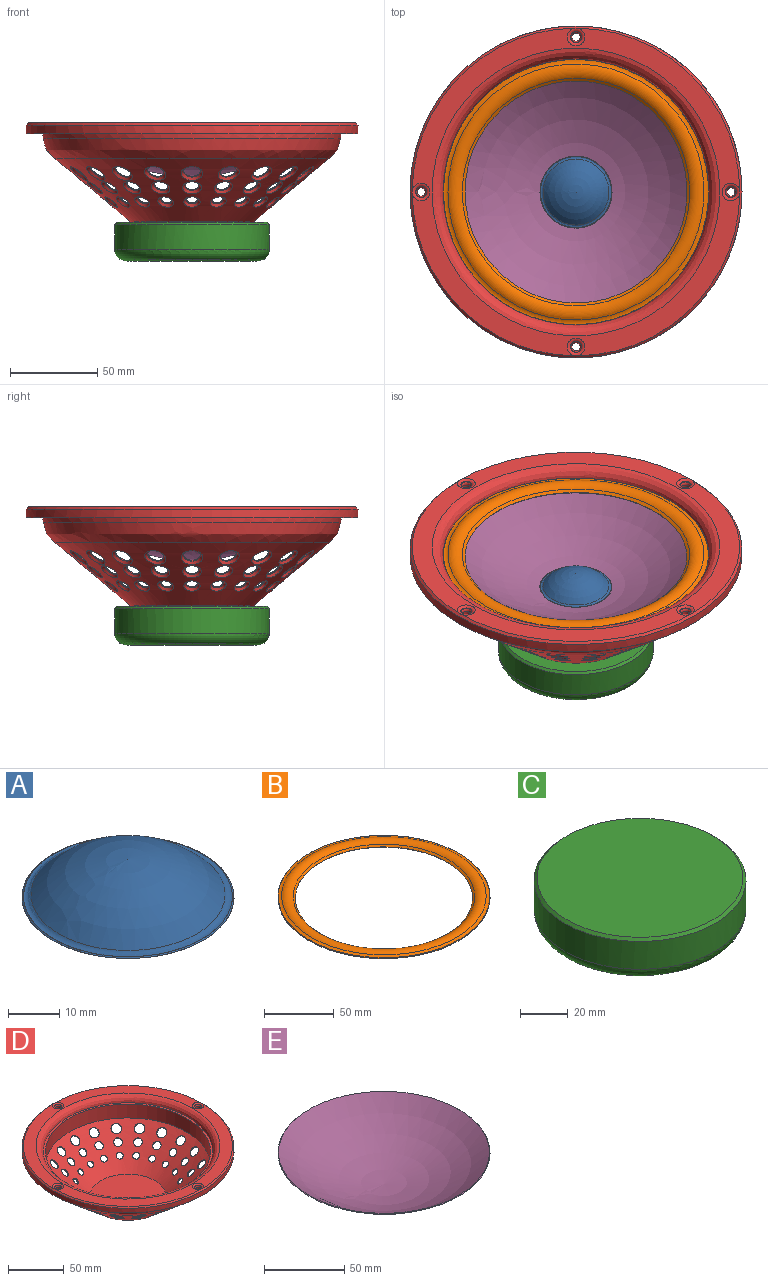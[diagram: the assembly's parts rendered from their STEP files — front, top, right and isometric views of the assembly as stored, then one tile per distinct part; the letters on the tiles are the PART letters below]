
ASSEMBLY  parts=5 mates=4
PART A: 7 faces, bbox 45.8x45.8x9.6 mm
  f0: sphere r=24.38mm, area 1308.1mm2, adj f1
  f1: sphere r=101.6mm, area 270.8mm2, adj f0,f2
  f2: cone r=20.64mm half-angle=11.7deg, axis (0,0,-1), area 0mm2, adj f1,f5
  f3: sphere r=101.35mm, area 2.8mm2, adj f5,f6
  f4: sphere r=25.4mm, area 1350.2mm2, adj f6
  f5: cone r=20.69mm half-angle=56.7deg, axis (0,0,-1), area 46.3mm2, adj f2,f3
  f6: torus R=20.06mm, axis (0,0,-1), area 195.8mm2, adj f3,f4
PART B: 9 faces, bbox 164.6x164.6x3.6 mm
  f0: torus R=69.85mm, axis (0,0,-1), area 4050mm2, adj f1,f7
  f1: plane 152.4x152.4mm, normal (0,0,-1), area 959.9mm2, adj f0,f2
  f2: cylinder r=76.2mm len=152.4mm, axis (0,0,-1), area 364.8mm2, adj f1,f3
  f3: plane 152.4x152.4mm, normal (0,0,1), area 73.1mm2, adj f2,f8
  f4: torus R=69.85mm, axis (0,0,-1), area 3828.5mm2, adj f5,f8
  f5: sphere r=100.84mm, area 823.2mm2, adj f4,f6
  f6: cone r=63.69mm half-angle=39.2deg, axis (0,0,-1), area 306.1mm2, adj f5,f7
  f7: sphere r=101.6mm, area 835.7mm2, adj f0,f6
  f8: torus R=76.05mm, axis (0,0,-1), area 1270.7mm2, adj f3,f4
PART C: 9 faces, bbox 97.6x97.6x22.2 mm
  f0: plane 86.36x86.36mm, normal (0,0,1), area 5857.5mm2, adj f8
  f1: sphere r=6.35mm, area 50.7mm2, adj f5
  f2: plane 51.04x51.04mm, normal (0,0,-1), area 1863.5mm2, adj f5,f6
  f3: torus R=36.05mm, axis (0,0,-1), area 2515.9mm2, adj f6,f7
  f4: cylinder r=44.45mm len=88.9mm, axis (0,0,-1), area 3984mm2, adj f7,f8
  f5: torus R=7.62mm, axis (0,0,1), area 145mm2, adj f1,f2
  f6: torus R=25.52mm, axis (0,0,-1), area 638.6mm2, adj f2,f3
  f7: torus R=38.1mm, axis (0,0,1), area 2127.8mm2, adj f3,f4
  f8: cone r=44.45mm half-angle=45deg, axis (0,0,-1), area 494.4mm2, adj f0,f4
PART D: 150 faces, bbox 192.7x190.5x57.2 mm
  f0: cone r=74.17mm half-angle=50deg, axis (0,0,1), area 14734.7mm2, adj f2,f9,f21,f22,f23,f24,f25,f26
  f1: cone r=84.05mm half-angle=50deg, axis (0,0,1), area 14756.1mm2, adj f18,f81,f82,f83,f84,f85,f86,f87
  f2: plane 68.23x68.23mm, normal (0,0,1), area 3656.6mm2, adj f0
  f3: plane 68.7x68.7mm, normal (0,0,-1), area 3706.4mm2, adj f141
  f4: cone r=85.72mm half-angle=10deg, axis (0,0,1), area 1470.8mm2, adj f5,f18
  f5: plane 190.5x190.5mm, normal (0,0,-1), area 5344.2mm2, adj f4,f6,f10,f12,f14,f16
  f6: cylinder r=95.25mm len=190.5mm, axis (0,0,-1), area 3040.2mm2, adj f5,f19
  f7: plane 187.99x187.99mm, normal (0,0,1), area 6016.8mm2, adj f19,f20,f143,f145,f147,f149
  f8: plane 152.41x152.41mm, normal (0,0,1), area 961.6mm2, adj f9,f20
  f9: cylinder r=74.17mm len=148.34mm, axis (0,0,-1), area 7065mm2, adj f0,f8
  f10: cylinder r=2.38mm len=4.76mm, axis (0,0,1), area 54.5mm2, adj f5,f148
  f11: cone r=2.38mm half-angle=42.5deg, axis (0,0,1), area 5.2mm2, adj f148,f149
  f12: cylinder r=2.38mm len=4.76mm, axis (0,0,1), area 54.5mm2, adj f5,f146
  f13: cone r=2.38mm half-angle=42.5deg, axis (0,0,1), area 5.2mm2, adj f146,f147
  f14: cylinder r=2.38mm len=4.76mm, axis (0,0,1), area 54.5mm2, adj f5,f144
  f15: cone r=2.38mm half-angle=42.5deg, axis (0,0,1), area 5.2mm2, adj f144,f145
  f16: cylinder r=2.38mm len=4.76mm, axis (0,0,1), area 54.5mm2, adj f5,f142
  f17: cone r=2.38mm half-angle=42.5deg, axis (0,0,1), area 5.2mm2, adj f142,f143
  f18: bspline ~170.5x170.5mm, area 7033.8mm2, adj f1,f4
  f19: cone r=95.25mm half-angle=45deg, axis (0,0,-1), area 1067.7mm2, adj f6,f7
  f20: bspline ~165.1x165.1mm, area 4895.7mm2, adj f7,f8
  f21: cylinder r=4.76mm len=9.53mm, axis (0.64,0,-0.77), area 17.4mm2, adj f0,f140
  f22: cylinder r=3.97mm len=7.62mm, axis (-0.38,0.52,-0.77), area 14.9mm2, adj f0,f118
  f23: cylinder r=4.76mm len=9.1mm, axis (-0.38,0.52,-0.77), area 17.9mm2, adj f0,f119
  f24: cylinder r=3.17mm len=6.11mm, axis (-0.38,0.52,-0.77), area 11.5mm2, adj f0,f117
  f25: cylinder r=4.76mm len=9.1mm, axis (-0.52,0.38,-0.77), area 19.6mm2, adj f0,f116
  f26: cylinder r=3.17mm len=6.35mm, axis (0,0.64,-0.77), area 11.3mm2, adj f0,f123
  f27: cylinder r=4.76mm len=9.48mm, axis (-0.2,0.61,-0.77), area 18mm2, adj f0,f122
  f28: cylinder r=3.17mm len=6.35mm, axis (-0.2,0.61,-0.77), area 11.5mm2, adj f0,f120
  f29: cylinder r=3.97mm len=7.91mm, axis (-0.2,0.61,-0.77), area 14.3mm2, adj f0,f121
  f30: cylinder r=3.17mm len=6.34mm, axis (-0.61,0.2,-0.77), area 11.3mm2, adj f0,f111
  f31: cylinder r=4.76mm len=9.53mm, axis (-0.64,0,-0.77), area 17.7mm2, adj f0,f110
  f32: cylinder r=3.97mm len=7.94mm, axis (-0.64,0,-0.77), area 14.8mm2, adj f0,f109
  f33: cylinder r=3.17mm len=6.35mm, axis (-0.64,0,-0.77), area 11.7mm2, adj f0,f108
  f34: cylinder r=3.17mm len=6.1mm, axis (-0.52,0.38,-0.77), area 11.4mm2, adj f0,f114
  f35: cylinder r=3.97mm len=7.62mm, axis (-0.52,0.38,-0.77), area 16mm2, adj f0,f115
  f36: cylinder r=3.97mm len=7.92mm, axis (-0.61,0.2,-0.77), area 16mm2, adj f0,f112
  f37: cylinder r=4.76mm len=9.48mm, axis (-0.61,0.2,-0.77), area 19.4mm2, adj f0,f113
  f38: cylinder r=3.17mm len=6.35mm, axis (0.61,0.2,-0.77), area 11.3mm2, adj f0,f135
  f39: cylinder r=4.76mm len=9.06mm, axis (0.52,0.38,-0.77), area 16.4mm2, adj f0,f134
  f40: cylinder r=3.17mm len=6.12mm, axis (0.52,0.38,-0.77), area 12.7mm2, adj f0,f132
  f41: cylinder r=3.97mm len=7.59mm, axis (0.52,0.38,-0.77), area 13.9mm2, adj f0,f133
  f42: cylinder r=4.76mm len=9.46mm, axis (0.61,0.2,-0.77), area 16.8mm2, adj f0,f137
  f43: cylinder r=3.97mm len=7.91mm, axis (0.61,0.2,-0.77), area 13.8mm2, adj f0,f136
  f44: cylinder r=3.17mm len=6.35mm, axis (0.64,0,-0.77), area 11.3mm2, adj f0,f138
  f45: cylinder r=3.97mm len=7.94mm, axis (0.64,0,-0.77), area 13.9mm2, adj f0,f139
  f46: cylinder r=4.76mm len=9.53mm, axis (0,0.64,-0.77), area 17.3mm2, adj f0,f125
  f47: cylinder r=3.97mm len=7.94mm, axis (0,0.64,-0.77), area 13.9mm2, adj f0,f124
  f48: cylinder r=3.97mm len=7.91mm, axis (0.2,0.61,-0.77), area 13.8mm2, adj f0,f127
  f49: cylinder r=3.17mm len=6.35mm, axis (0.2,0.61,-0.77), area 11.3mm2, adj f0,f126
  f50: cylinder r=3.97mm len=7.59mm, axis (0.38,0.52,-0.77), area 13.9mm2, adj f0,f130
  f51: cylinder r=4.76mm len=9.06mm, axis (0.38,0.52,-0.77), area 16.4mm2, adj f0,f131
  f52: cylinder r=3.17mm len=6.12mm, axis (0.38,0.52,-0.77), area 12.7mm2, adj f0,f129
  f53: cylinder r=4.76mm len=9.46mm, axis (0.2,0.61,-0.77), area 16.8mm2, adj f0,f128
  f54: cylinder r=3.17mm len=6.13mm, axis (0.38,-0.52,-0.77), area 12.1mm2, adj f0,f87
  f55: cylinder r=4.76mm len=9.1mm, axis (0.52,-0.38,-0.77), area 18mm2, adj f0,f86
  f56: cylinder r=3.17mm len=6.13mm, axis (0.52,-0.38,-0.77), area 11.8mm2, adj f0,f84
  f57: cylinder r=3.97mm len=7.62mm, axis (0.52,-0.38,-0.77), area 14.9mm2, adj f0,f85
  f58: cylinder r=4.76mm len=9.1mm, axis (0.38,-0.52,-0.77), area 19.5mm2, adj f0,f89
  f59: cylinder r=3.97mm len=7.62mm, axis (0.38,-0.52,-0.77), area 16mm2, adj f0,f88
  f60: cylinder r=3.97mm len=7.92mm, axis (0.2,-0.61,-0.77), area 16mm2, adj f0,f91
  f61: cylinder r=3.17mm len=6.36mm, axis (0.2,-0.61,-0.77), area 12.3mm2, adj f0,f90
  f62: cylinder r=3.17mm len=6.35mm, axis (0.61,-0.2,-0.77), area 11.5mm2, adj f0,f81
  f63: cylinder r=4.76mm len=9.48mm, axis (0.61,-0.2,-0.77), area 17.9mm2, adj f0,f83
  f64: cylinder r=3.97mm len=7.91mm, axis (0.61,-0.2,-0.77), area 14.3mm2, adj f0,f82
  f65: cylinder r=4.76mm len=9.06mm, axis (-0.38,-0.52,-0.77), area 16.3mm2, adj f0,f101
  f66: cylinder r=3.97mm len=7.61mm, axis (-0.38,-0.52,-0.77), area 15.3mm2, adj f0,f100
  f67: cylinder r=3.97mm len=7.61mm, axis (-0.52,-0.38,-0.77), area 15.2mm2, adj f0,f103
  f68: cylinder r=3.17mm len=6.1mm, axis (-0.52,-0.38,-0.77), area 11.2mm2, adj f0,f102
  f69: cylinder r=3.97mm len=7.92mm, axis (-0.61,-0.2,-0.77), area 15.8mm2, adj f0,f106
  f70: cylinder r=4.76mm len=9.48mm, axis (-0.61,-0.2,-0.77), area 19.3mm2, adj f0,f107
  f71: cylinder r=3.17mm len=6.36mm, axis (-0.61,-0.2,-0.77), area 12.5mm2, adj f0,f105
  f72: cylinder r=4.76mm len=9.06mm, axis (-0.52,-0.38,-0.77), area 16.4mm2, adj f0,f104
  f73: cylinder r=3.97mm len=7.92mm, axis (-0.2,-0.61,-0.77), area 15.8mm2, adj f0,f97
  f74: cylinder r=3.17mm len=6.36mm, axis (-0.2,-0.61,-0.77), area 12.5mm2, adj f0,f96
  f75: cylinder r=4.76mm len=9.48mm, axis (-0.2,-0.61,-0.77), area 19.3mm2, adj f0,f98
  f76: cylinder r=3.17mm len=6.14mm, axis (-0.38,-0.52,-0.77), area 12.3mm2, adj f0,f99
  f77: cylinder r=4.76mm len=9.48mm, axis (0.2,-0.61,-0.77), area 19.5mm2, adj f0,f92
  f78: cylinder r=3.17mm len=6.35mm, axis (0,-0.64,-0.77), area 12.6mm2, adj f0,f93
  f79: cylinder r=4.76mm len=9.53mm, axis (0,-0.64,-0.77), area 19.5mm2, adj f0,f95
  f80: cylinder r=3.97mm len=7.94mm, axis (0,-0.64,-0.77), area 16.1mm2, adj f0,f94
  f81: bspline ~9.11x7.25mm, area 49mm2, adj f1,f62
  f82: bspline ~10.66x8.51mm, area 59mm2, adj f1,f64
  f83: bspline ~12.21x9.76mm, area 68.9mm2, adj f1,f63
  f84: bspline ~8.58x7.87mm, area 49mm2, adj f1,f56
  f85: bspline ~10.04x9.23mm, area 59mm2, adj f1,f57
  f86: bspline ~11.51x10.58mm, area 68.9mm2, adj f1,f55
  f87: bspline ~8.58x7.88mm, area 49mm2, adj f1,f54
  f88: bspline ~10.05x9.23mm, area 59mm2, adj f1,f59
  f89: bspline ~11.51x10.58mm, area 68.9mm2, adj f1,f58
  f90: bspline ~9.11x7.25mm, area 49mm2, adj f1,f61
  f91: bspline ~10.66x8.51mm, area 59mm2, adj f1,f60
  f92: bspline ~12.21x9.76mm, area 68.9mm2, adj f1,f77
  f93: bspline ~9.3x7mm, area 49mm2, adj f1,f78
  f94: bspline ~10.88x8.21mm, area 58.9mm2, adj f1,f80
  f95: bspline ~12.47x9.42mm, area 68.9mm2, adj f1,f79
  f96: bspline ~9.11x7.25mm, area 49mm2, adj f1,f74
  f97: bspline ~10.66x8.51mm, area 58.9mm2, adj f1,f73
  f98: bspline ~12.21x9.76mm, area 68.9mm2, adj f1,f75
  f99: bspline ~8.59x7.88mm, area 49mm2, adj f1,f76
  f100: bspline ~10.04x9.22mm, area 59mm2, adj f1,f66
  f101: bspline ~11.51x10.58mm, area 68.9mm2, adj f1,f65
  f102: bspline ~8.59x7.88mm, area 49mm2, adj f1,f68
  f103: bspline ~10.04x9.22mm, area 59mm2, adj f1,f67
  f104: bspline ~11.51x10.58mm, area 68.9mm2, adj f1,f72
  f105: bspline ~9.11x7.25mm, area 49mm2, adj f1,f71
  f106: bspline ~10.66x8.51mm, area 59mm2, adj f1,f69
  f107: bspline ~12.21x9.76mm, area 68.9mm2, adj f1,f70
  f108: bspline ~9.3x7mm, area 49mm2, adj f1,f33
  f109: bspline ~10.89x8.21mm, area 59mm2, adj f1,f32
  f110: bspline ~12.47x9.43mm, area 69mm2, adj f1,f31
  f111: bspline ~9.11x7.25mm, area 49mm2, adj f1,f30
  f112: bspline ~10.66x8.51mm, area 59mm2, adj f1,f36
  f113: bspline ~12.21x9.76mm, area 68.9mm2, adj f1,f37
  f114: bspline ~8.58x7.88mm, area 49mm2, adj f1,f34
  f115: bspline ~10.05x9.23mm, area 59mm2, adj f1,f35
  f116: bspline ~11.51x10.58mm, area 68.9mm2, adj f1,f25
  f117: bspline ~8.58x7.87mm, area 49mm2, adj f1,f24
  f118: bspline ~10.04x9.23mm, area 58.9mm2, adj f1,f22
  f119: bspline ~11.51x10.58mm, area 68.9mm2, adj f1,f23
  f120: bspline ~9.11x7.25mm, area 49mm2, adj f1,f28
  f121: bspline ~10.66x8.51mm, area 59mm2, adj f1,f29
  f122: bspline ~12.21x9.76mm, area 68.9mm2, adj f1,f27
  f123: bspline ~9.3x7mm, area 49mm2, adj f1,f26
  f124: bspline ~10.89x8.21mm, area 59mm2, adj f1,f47
  f125: bspline ~12.47x9.43mm, area 68.9mm2, adj f1,f46
  f126: bspline ~9.1x7.25mm, area 49mm2, adj f1,f49
  f127: bspline ~10.66x8.51mm, area 59mm2, adj f1,f48
  f128: bspline ~12.21x9.76mm, area 68.9mm2, adj f1,f53
  f129: bspline ~8.58x7.88mm, area 49mm2, adj f1,f52
  f130: bspline ~10.05x9.23mm, area 59mm2, adj f1,f50
  f131: bspline ~11.52x10.59mm, area 68.9mm2, adj f1,f51
  f132: bspline ~8.58x7.88mm, area 49mm2, adj f1,f40
  f133: bspline ~10.05x9.23mm, area 59mm2, adj f1,f41
  f134: bspline ~11.52x10.59mm, area 68.9mm2, adj f1,f39
  f135: bspline ~9.1x7.25mm, area 49mm2, adj f1,f38
  f136: bspline ~10.66x8.51mm, area 59mm2, adj f1,f43
  f137: bspline ~12.21x9.76mm, area 68.9mm2, adj f1,f42
  f138: bspline ~9.3x7mm, area 49mm2, adj f1,f44
  f139: bspline ~10.89x8.21mm, area 59mm2, adj f1,f45
  f140: bspline ~12.47x9.43mm, area 68.9mm2, adj f1,f21
  f141: cone r=34.35mm half-angle=70deg, axis (0,0,1), area 208.7mm2, adj f1,f3
  f142: torus R=4.9mm, axis (0,0,-1), area 30.5mm2, adj f16,f17
  f143: torus R=5.08mm, axis (0,0,1), area 53.6mm2, adj f7,f17
  f144: torus R=4.9mm, axis (0,0,-1), area 30.5mm2, adj f14,f15
  f145: torus R=5.08mm, axis (0,0,1), area 53.6mm2, adj f7,f15
  f146: torus R=4.9mm, axis (0,0,-1), area 30.5mm2, adj f12,f13
  f147: torus R=5.08mm, axis (0,0,1), area 53.6mm2, adj f7,f13
  f148: torus R=4.9mm, axis (0,0,-1), area 30.5mm2, adj f10,f11
  f149: torus R=5.08mm, axis (0,0,1), area 53.6mm2, adj f7,f11
PART E: 3 faces, bbox 132.1x132.1x24.6 mm
  f0: sphere r=101.6mm, area 15410.2mm2, adj f2
  f1: sphere r=102.11mm, area 15564.7mm2, adj f2
  f2: cone r=65.75mm half-angle=40.3deg, axis (0,0,-1), area 210.4mm2, adj f0,f1
PLACE A t=(0,0,-19.05)mm
PLACE B t=(0,0,-19.05)mm
PLACE C t=(0,0,-19.05)mm
PLACE D t=(0,0,-19.05)mm
PLACE E t=(0,0,-19.05)mm
MATE fastened C.f3 <-> D.f0  axis (0,0,1) through (0,0,0)mm
MATE fastened B.f0 <-> D.f0  axis (0,0,-1) through (0,0,50.8)mm
MATE planar E.f2 <-> B.f0  axis (0,0,1) through (0,0,128.44)mm
MATE planar E.f2 <-> A.f2  axis (0,0,1) through (0,0,128.44)mm
